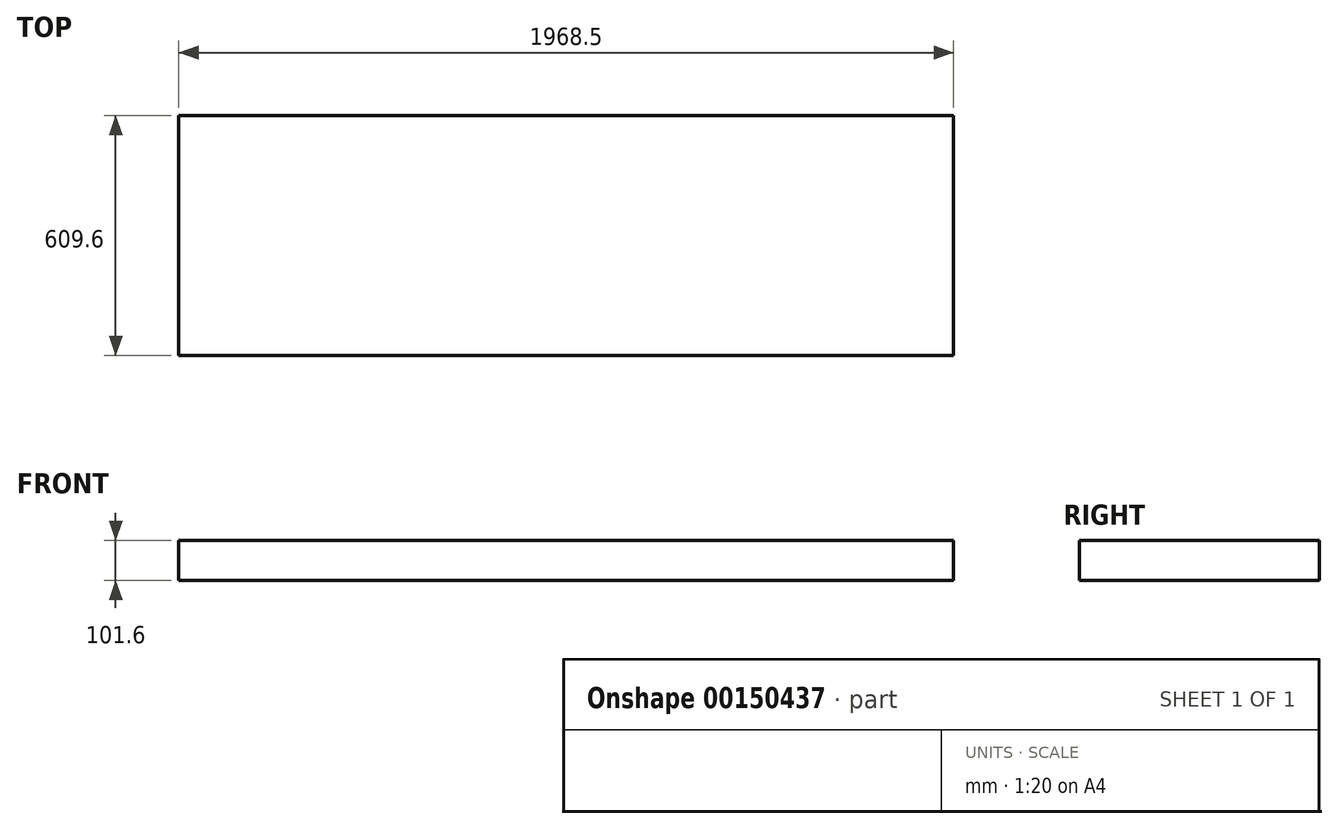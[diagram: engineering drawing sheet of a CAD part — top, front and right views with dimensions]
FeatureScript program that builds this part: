
annotation { "Feature Type Name" : "Feature", "Feature Type Description" : "" }
export const myFeature = defineFeature(function(context is Context, id is Id, definition is map)
    precondition{}
    {
        {
            var Q0;
            Q0=qCreatedBy(makeId("Top.planeOp"), FACE);
            var sketch = newSketch(context, id + "F0", { "sketchPlane" : qUnion([Q0])});
            skLineSegment(sketch, "E0.bottom", {"start": v(984.25, 304.8) * mm, "end": v(-984.25, 304.8) * mm});
            skLineSegment(sketch, "E0.top", {"start": v(984.25, -304.8) * mm, "end": v(-984.25, -304.8) * mm});
            skLineSegment(sketch, "E0.left", {"start": v(984.25, 304.8) * mm, "end": v(984.25, -304.8) * mm});
            skLineSegment(sketch, "E0.right", {"start": v(-984.25, 304.8) * mm, "end": v(-984.25, -304.8) * mm});
            skPoint(sketch, "E0.middle", {"position": v(0, 0) * mm});
            skSolve(sketch);
        }
        {
            var Q0;
            Q0 = qSketchRegion(id + "F0", true);
            extrude(context, id + "F1", {"entities" : qUnion([Q0]), "depth" : 101.6 * mm, "offsetDistance" : 25.4 * mm});
        }
    });
